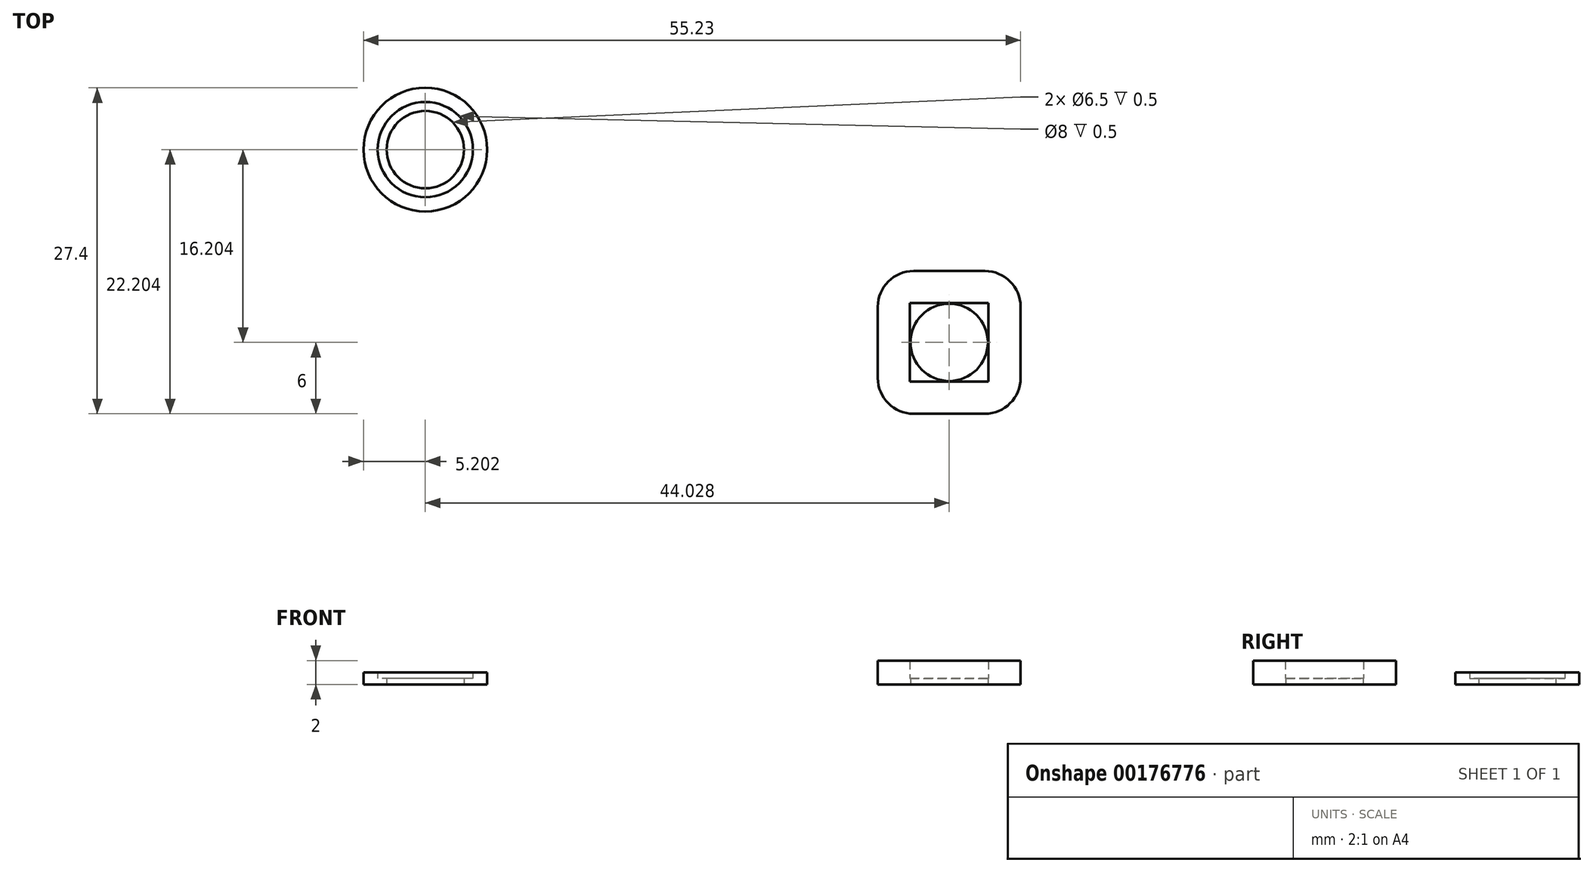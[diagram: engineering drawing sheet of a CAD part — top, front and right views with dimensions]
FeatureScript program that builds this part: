
annotation { "Feature Type Name" : "Feature", "Feature Type Description" : "" }
export const myFeature = defineFeature(function(context is Context, id is Id, definition is map)
    precondition{}
    {
        {
            assignVariable(context, id + "F0", {"name" : "frameThickness", "anyValue" : 2});
        }
        {
            assignVariable(context, id + "F1", {"name" : "threadGap", "anyValue" : 3});
        }
        {
            assignVariable(context, id + "F2", {"name" : "mountSquareThickness", "anyValue" : 1.5});
        }
        {
            var Q0;
            Q0=qCreatedBy(makeId("Top.planeOp"),FACE);
            var sketch = newSketch(context, id + "F3", { "sketchPlane" : qUnion([Q0])});
            skLineSegment(sketch, "E0.bottom", {"start": v(-6, 6) * mm, "end": v(6, 6) * mm});
            skLineSegment(sketch, "E0.top", {"start": v(-6, -6) * mm, "end": v(6, -6) * mm});
            skLineSegment(sketch, "E0.left", {"start": v(-6, 6) * mm, "end": v(-6, -6) * mm});
            skLineSegment(sketch, "E0.right", {"start": v(6, 6) * mm, "end": v(6, -6) * mm});
            skPoint(sketch, "E0.middle", {"position": v(0, 0) * mm});
            skCircle(sketch, "E1", {"center": v(0, 0) * mm, "radius": 3.25 * mm});
            skSolve(sketch);
        }
        {
            var Q0;
            Q0 = qSketchRegion(id + "F3", true);
            extrude(context, id + "F4", {"entities" : qUnion([Q0]), "depth" : (getVariable(context, 'threadGap') - getVariable(context, 'frameThickness')) / 2 * mm});
        }
        {
            var Q0;
            Q0=makeQuery(id+"F4.opExtrude","CAP_FACE",FACE,{"disambiguationData":[OSD([sQuery(id+"F3.wireOp",EDGE,"E0.bottom"),sQuery(id+"F3.wireOp",EDGE,"E0.top"),sQuery(id+"F3.wireOp",EDGE,"E0.left"),sQuery(id+"F3.wireOp",EDGE,"E0.right"),sQuery(id+"F3.wireOp",EDGE,"E1")])],"isStart":false});
            var sketch = newSketch(context, id + "F5", { "sketchPlane" : qUnion([Q0])});
            skLineSegment(sketch, "E2.bottom", {"start": v(-3.3, 3.3) * mm, "end": v(3.3, 3.3) * mm});
            skLineSegment(sketch, "E2.top", {"start": v(-3.3, -3.3) * mm, "end": v(3.3, -3.3) * mm});
            skLineSegment(sketch, "E2.left", {"start": v(-3.3, 3.3) * mm, "end": v(-3.3, -3.3) * mm});
            skLineSegment(sketch, "E2.right", {"start": v(3.3, 3.3) * mm, "end": v(3.3, -3.3) * mm});
            skPoint(sketch, "E2.middle", {"position": v(0, 0) * mm});
            skLineSegment(sketch, "E3.bottom", {"start": v(-6, 6) * mm, "end": v(6, 6) * mm});
            skLineSegment(sketch, "E3.top", {"start": v(-6, -6) * mm, "end": v(6, -6) * mm});
            skLineSegment(sketch, "E3.left", {"start": v(-6, 6) * mm, "end": v(-6, -6) * mm});
            skLineSegment(sketch, "E3.right", {"start": v(6, 6) * mm, "end": v(6, -6) * mm});
            skSolve(sketch);
        }
        {
            var Q0;
            Q0 = qSketchRegion(id + "F5", true);
            extrude(context, id + "F6", {"entities" : qUnion([Q0]), "operationType" : NewBodyOperationType.ADD, "depth" : (getVariable(context, 'mountSquareThickness')) * mm});
        }
        {
            var Q0;
            Q0=makeQuery(id+"F6.boolean.opBoolean","MERGE",EDGE,{"derivedFrom":[makeQuery(id+"F4.opExtrude","SWEPT_EDGE",EDGE,{"disambiguationData":[OSD([sQuery(id+"F3.wireOp",EDGE,"E0.bottom"),sQuery(id+"F3.wireOp",EDGE,"E0.left")])]}),makeQuery(id+"F6.opExtrude","SWEPT_EDGE",EDGE,{"disambiguationData":[OSD([sQuery(id+"F5.wireOp",EDGE,"E3.bottom"),sQuery(id+"F5.wireOp",EDGE,"E3.left")])]})]});
            var Q1;
            Q1=makeQuery(id+"F6.boolean.opBoolean","MERGE",EDGE,{"derivedFrom":[makeQuery(id+"F4.opExtrude","SWEPT_EDGE",EDGE,{"disambiguationData":[OSD([sQuery(id+"F3.wireOp",EDGE,"E0.bottom"),sQuery(id+"F3.wireOp",EDGE,"E0.right")])]}),makeQuery(id+"F6.opExtrude","SWEPT_EDGE",EDGE,{"disambiguationData":[OSD([sQuery(id+"F5.wireOp",EDGE,"E3.bottom"),sQuery(id+"F5.wireOp",EDGE,"E3.right")])]})]});
            var Q2;
            Q2=makeQuery(id+"F6.boolean.opBoolean","MERGE",EDGE,{"derivedFrom":[makeQuery(id+"F4.opExtrude","SWEPT_EDGE",EDGE,{"disambiguationData":[OSD([sQuery(id+"F3.wireOp",EDGE,"E0.top"),sQuery(id+"F3.wireOp",EDGE,"E0.right")])]}),makeQuery(id+"F6.opExtrude","SWEPT_EDGE",EDGE,{"disambiguationData":[OSD([sQuery(id+"F5.wireOp",EDGE,"E3.top"),sQuery(id+"F5.wireOp",EDGE,"E3.right")])]})]});
            var Q3;
            Q3=makeQuery(id+"F6.boolean.opBoolean","MERGE",EDGE,{"derivedFrom":[makeQuery(id+"F4.opExtrude","SWEPT_EDGE",EDGE,{"disambiguationData":[OSD([sQuery(id+"F3.wireOp",EDGE,"E0.top"),sQuery(id+"F3.wireOp",EDGE,"E0.left")])]}),makeQuery(id+"F6.opExtrude","SWEPT_EDGE",EDGE,{"disambiguationData":[OSD([sQuery(id+"F5.wireOp",EDGE,"E3.top"),sQuery(id+"F5.wireOp",EDGE,"E3.left")])]})]});
            fillet(context, id + "F7", {"entities" : qUnion([Q0, Q1, Q2, Q3]), "radius" : 3 * mm, "tangentPropagation" : true, "allowEdgeOverflow" : false});
        }
        {
            var Q0;
            Q0=qCreatedBy(makeId("Top.planeOp"),FACE);
            var sketch = newSketch(context, id + "F8", { "sketchPlane" : qUnion([Q0])});
            skCircle(sketch, "E4", {"center": v(-44.03, 16.2) * mm, "radius": 4 * mm});
            skCircle(sketch, "E5", {"center": v(-44.03, 16.2) * mm, "radius": 3.25 * mm});
            skCircle(sketch, "E6", {"center": v(-44.03, 16.2) * mm, "radius": 5.2 * mm});
            skSolve(sketch);
        }
        {
            var Q0;
            Q0 = qSketchRegion(id + "F8", true);
            extrude(context, id + "F9", {"entities" : qUnion([Q0]), "depth" : 1 * mm});
        }
        {
            var Q0;
            Q0=makeQuery(id+"F8.imprint","IMPRINT",FACE,{"disambiguationData":[TD([[makeQuery(id+"F8.imprint","IMPRINT",EDGE,{"derivedFrom":sQuery(id+"F8.wireOp",EDGE,"E4")}),1.0]])]});
            extrude(context, id + "F10", {"entities" : qUnion([Q0]), "operationType" : NewBodyOperationType.ADD, "depth" : 0.5 * mm});
        }
    });
